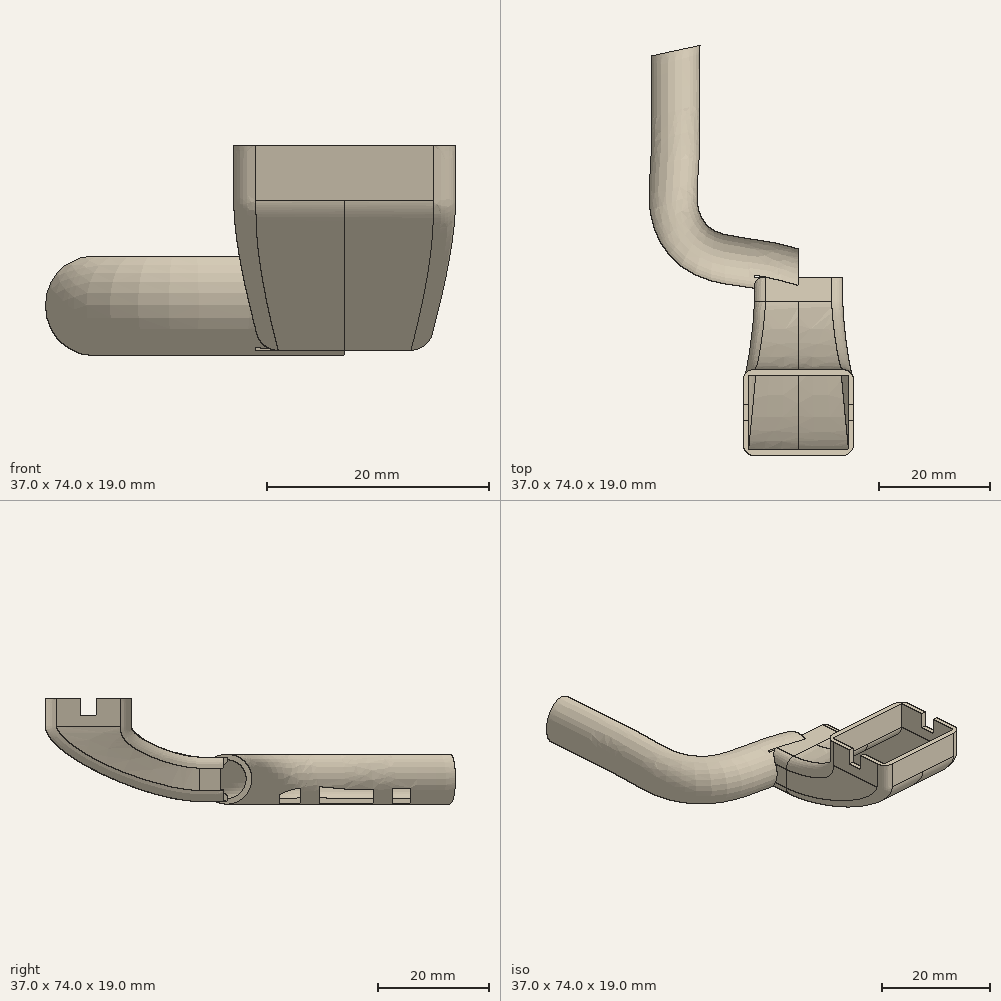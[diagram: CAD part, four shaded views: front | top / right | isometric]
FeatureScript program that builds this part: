
annotation { "Feature Type Name" : "Feature", "Feature Type Description" : "" }
export const myFeature = defineFeature(function(context is Context, id is Id, definition is map)
    precondition{}
    {
        {
            var Q0;
            Q0=qCreatedBy(makeId("Top.planeOp"),FACE);
            var sketch = newSketch(context, id + "F0", { "sketchPlane" : qUnion([Q0])});
            skLineSegment(sketch, "E0.bottom", {"start": v(-10, -17.25) * mm, "end": v(0, -17.25) * mm});
            skLineSegment(sketch, "E0.top", {"start": v(-10, -32.75) * mm, "end": v(0, -32.75) * mm});
            skLineSegment(sketch, "E0.left", {"start": v(-10, -17.25) * mm, "end": v(-10, -32.75) * mm});
            skLineSegment(sketch, "E0.right", {"start": v(0, -17.25) * mm, "end": v(0, -32.75) * mm});
            skPoint(sketch, "E0.middle", {"position": v(-5, -25) * mm});
            skSolve(sketch);
        }
        {
            var Q0;
            Q0=qCreatedBy(makeId("Front.planeOp"),FACE);
            var sketch = newSketch(context, id + "F1", { "sketchPlane" : qUnion([Q0])});
            skLineSegment(sketch, "E1", {"start": v(-4.94, -14.5) * mm, "end": v(6.87, -14.5) * mm, "construction": true});
            skLineSegment(sketch, "E2.bottom", {"start": v(-8, -10.5) * mm, "end": v(0, -10.5) * mm});
            skLineSegment(sketch, "E2.top", {"start": v(-8, -18.5) * mm, "end": v(0, -18.5) * mm});
            skLineSegment(sketch, "E2.left", {"start": v(-8, -10.5) * mm, "end": v(-8, -18.5) * mm});
            skPoint(sketch, "E2.middle", {"position": v(0, -14.5) * mm});
            skLineSegment(sketch, "E3", {"start": v(0, 0) * mm, "end": v(0, -51.5) * mm, "construction": true});
            skPoint(sketch, "E3.endSnap0", {"position": v(0, -18.5) * mm});
            skLineSegment(sketch, "E4", {"start": v(0, -51.5) * mm, "end": v(0, 0) * mm, "construction": true});
            skLineSegment(sketch, "E5", {"start": v(0, 46.65) * mm, "end": v(0, 0) * mm, "construction": true});
            skLineSegment(sketch, "E6", {"start": v(0, -10.5) * mm, "end": v(0, -18.5) * mm});
            skPoint(sketch, "E7.orphan", {"position": v(8, -10.5) * mm});
            skPoint(sketch, "E8.orphan", {"position": v(8, -18.5) * mm});
            skSolve(sketch);
        }
        {
            var Q0;
            Q0=qCreatedBy(makeId("Right.planeOp"),FACE);
            var sketch = newSketch(context, id + "F2", { "sketchPlane" : qUnion([Q0])});
            skCircle(sketch, "E9", {"center": v(0, -14.5) * mm, "radius": 4.5 * mm});
            skSolve(sketch);
        }
        {
            var Q0;
            Q0=sQuery(id+"F1.wireOp",EDGE,"E1");
            cPlane(context, id + "F3", {"entities" : qUnion([Q0]), "cplaneType" : CPlaneType.LINE_ANGLE, "offset" : 25 * mm, "angle" : 90 * degree, "width" : 150 * mm, "height" : 150 * mm});
        }
        {
            var Q0;
            Q0=qCreatedBy(id+"F3.planeOp",FACE);
            var sketch = newSketch(context, id + "F4", { "sketchPlane" : qUnion([Q0])});
            skFitSpline(sketch, "E10", {"points": [v(0, 0) * mm, v(-3.6, 0.99) * mm, v(-9.1, 2) * mm, v(-17.4, 4.14) * mm, v(-22.17, 10.6) * mm, v(-22.33, 20.29) * mm, v(-22.17, 29.36) * mm, v(-22.17, 36.59) * mm, v(-22.17, 40.28) * mm], "startDerivative": vector(-34.67, 9.15) * mm, "endDerivative": vector(2.11, 46.5) * mm});
            skLineSegment(sketch, "E11", {"start": v(0, 0) * mm, "end": v(0, 49.73) * mm, "construction": true});
            skSolve(sketch);
        }
        {
            var Q0;
            Q0=sQuery(id+"F4.wireOp",VERTEX,"E10.8.internal");
            var Q1;
            Q1=sQuery(id+"F4.wireOp",EDGE,"E11");
            cPlane(context, id + "F5", {"entities" : qUnion([Q0, Q1]), "cplaneType" : CPlaneType.LINE_POINT, "offset" : 25 * mm, "width" : 150 * mm, "height" : 150 * mm});
        }
        {
            var Q0;
            Q0=sQuery(id+"F1.wireOp",EDGE,"E2.bottom");
            cPlane(context, id + "F6", {"entities" : qUnion([Q0]), "cplaneType" : CPlaneType.LINE_ANGLE, "offset" : 25 * mm, "angle" : 27.84 * degree, "width" : 150 * mm, "height" : 150 * mm});
        }
        {
            var Q0;
            Q0 = qSketchRegion(id + "F0", true);
            extrude(context, id + "F7", {"entities" : qUnion([Q0]), "oppositeDirection" : true, "depth" : 5 * mm});
        }
        {
            var Q0;
            Q0=makeQuery(id+"F2.imprint","IMPRINT",FACE,{"disambiguationData":[TD([[makeQuery(id+"F2.imprint","IMPRINT",EDGE,{"derivedFrom":sQuery(id+"F2.wireOp",EDGE,"E9")}),1.0]])]});
            var Q1;
            Q1=sQuery(id+"F2.wireOp",EDGE,"E9");
            var Q2;
            Q2=sQuery(id+"F4.wireOp",EDGE,"E10");
            sweep(context, id + "F8", {"profiles" : qUnion([Q0]), "surfaceProfiles" : qUnion([Q1]), "path" : qUnion([Q2])});
        }
        {
            var Q0;
            Q0 = qSketchRegion(id + "F1", true);
            extrude(context, id + "F9", {"entities" : qUnion([Q0]), "depth" : 5 * mm});
        }
        {
            var Q0;
            Q0=makeQuery(id+"F9.opExtrude","SWEPT_FACE",FACE,{"disambiguationData":[OSD([sQuery(id+"F1.wireOp",EDGE,"E6")])]});
            var Q1;
            Q1=makeQuery(id+"F9.opExtrude","CAP_FACE",FACE,{"disambiguationData":[OSD([sQuery(id+"F1.wireOp",EDGE,"E2.bottom"),sQuery(id+"F1.wireOp",EDGE,"E2.top"),sQuery(id+"F1.wireOp",EDGE,"E2.left"),sQuery(id+"F1.wireOp",EDGE,"E6")])],"isStart":true});
            var Q2;
            Q2=makeQuery(id+"F9.opExtrude","SWEPT_BODY",BODY,{"disambiguationData":[OSD([sQuery(id+"F1.wireOp",EDGE,"E2.bottom"),sQuery(id+"F1.wireOp",EDGE,"E2.top"),sQuery(id+"F1.wireOp",EDGE,"E2.left"),sQuery(id+"F1.wireOp",EDGE,"E6")])]});
            shell(context, id + "F10", {"entities" : qUnion([Q0, Q1]), "parts" : qUnion([Q2]), "thickness" : 1 * mm});
        }
        {
            var Q0;
            Q0=makeQuery(id+"F7.opExtrude","CAP_FACE",FACE,{"disambiguationData":[OSD([sQuery(id+"F0.wireOp",EDGE,"E0.bottom"),sQuery(id+"F0.wireOp",EDGE,"E0.top"),sQuery(id+"F0.wireOp",EDGE,"E0.left"),sQuery(id+"F0.wireOp",EDGE,"E0.right")])],"isStart":false});
            var Q1;
            Q1=makeQuery(id+"F9.opExtrude","CAP_FACE",FACE,{"disambiguationData":[OSD([sQuery(id+"F1.wireOp",EDGE,"E2.bottom"),sQuery(id+"F1.wireOp",EDGE,"E2.top"),sQuery(id+"F1.wireOp",EDGE,"E2.left"),sQuery(id+"F1.wireOp",EDGE,"E6")])],"isStart":false});
            loft(context, id + "F11", {"startCondition" : LoftEndDerivativeType.NORMAL_TO_PROFILE, "startMagnitude" : 1, "endCondition" : LoftEndDerivativeType.NORMAL_TO_PROFILE, "endMagnitude" : 1, "sheetProfilesArray" : [{ "sheetProfileEntities" : qUnion([Q0]) }, { "sheetProfileEntities" : qUnion([Q1]) }]});
        }
        {
            var Q0;
            Q0=makeQuery(id+"F8.opSweep","CAP_FACE",FACE,{"disambiguationData":[OSD([sQuery(id+"F2.wireOp",EDGE,"E9"),sQuery(id+"F4.wireOp",VERTEX,"E10.start")])],"isStart":true});
            shell(context, id + "F12", {"entities" : qUnion([Q0]), "thickness" : 1 * mm});
        }
        {
            var Q0;
            Q0=makeQuery(id+"F1.imprint","IMPRINT",FACE,{"disambiguationData":[TD([[makeQuery(id+"F1.imprint","IMPRINT",EDGE,{"derivedFrom":sQuery(id+"F1.wireOp",EDGE,"E2.bottom")}),-1.0]])]});
            extrude(context, id + "F13", {"entities" : qUnion([Q0]), "operationType" : NewBodyOperationType.REMOVE, "depth" : 0.6 * mm});
        }
        {
            var Q0;
            Q0=makeQuery(id+"F7.opExtrude","SWEPT_BODY",BODY,{"disambiguationData":[OSD([sQuery(id+"F0.wireOp",EDGE,"E0.bottom"),sQuery(id+"F0.wireOp",EDGE,"E0.top"),sQuery(id+"F0.wireOp",EDGE,"E0.left"),sQuery(id+"F0.wireOp",EDGE,"E0.right")])]});
            var Q1;
            Q1=makeQuery(id+"F11.opLoft","SWEPT_BODY",BODY,{"disambiguationData":[OSD([sQuery(id+"F0.wireOp",EDGE,"E0.bottom"),sQuery(id+"F0.wireOp",EDGE,"E0.top"),sQuery(id+"F0.wireOp",EDGE,"E0.left"),sQuery(id+"F0.wireOp",EDGE,"E0.right"),sQuery(id+"F1.wireOp",EDGE,"E2.bottom"),sQuery(id+"F1.wireOp",EDGE,"E2.top"),sQuery(id+"F1.wireOp",EDGE,"E2.left"),sQuery(id+"F1.wireOp",EDGE,"E6")])]});
            var Q2;
            Q2=makeQuery(id+"F9.opExtrude","SWEPT_BODY",BODY,{"disambiguationData":[OSD([sQuery(id+"F1.wireOp",EDGE,"E2.bottom"),sQuery(id+"F1.wireOp",EDGE,"E2.top"),sQuery(id+"F1.wireOp",EDGE,"E2.left"),sQuery(id+"F1.wireOp",EDGE,"E6")])]});
            booleanBodies(context, id + "F14", {"operationType" : BooleanOperationType.UNION, "tools" : qUnion([Q0, Q1, Q2])});
        }
        {
            var Q0;
            {var subQ0=sQuery(id+"F1.wireOp",EDGE,"E6");var subQ1=sQuery(id+"F0.wireOp",EDGE,"E0.right");Q0=makeQuery(id+"F14.opBoolean","MERGE",FACE,{"derivedFrom":[makeQuery(id+"F7.opExtrude","SWEPT_FACE",FACE,{"disambiguationData":[OSD([subQ1])]}),makeQuery(id+"F11.opLoft","SWEPT_FACE",FACE,{"disambiguationData":[OSD([sQuery(id+"F0.wireOp",EDGE,"E0.bottom"),sQuery(id+"F0.wireOp",EDGE,"E0.top"),subQ1,sQuery(id+"F1.wireOp",EDGE,"E2.bottom"),sQuery(id+"F1.wireOp",EDGE,"E2.top"),subQ0])]}),makeQuery(id+"F9.opExtrude","SWEPT_FACE",FACE,{"disambiguationData":[OSD([subQ0])]})]});}
            var Q1;
            Q1=makeQuery(id+"F10.opShell","OFFSET_FACE",FACE,{"disambiguationData":[OSD([sQuery(id+"F1.wireOp",EDGE,"E2.bottom"),sQuery(id+"F1.wireOp",EDGE,"E2.top"),sQuery(id+"F1.wireOp",EDGE,"E2.left"),sQuery(id+"F1.wireOp",EDGE,"E6")])]});
            var Q2;
            Q2=makeQuery(id+"F7.opExtrude","CAP_FACE",FACE,{"disambiguationData":[OSD([sQuery(id+"F0.wireOp",EDGE,"E0.bottom"),sQuery(id+"F0.wireOp",EDGE,"E0.top"),sQuery(id+"F0.wireOp",EDGE,"E0.left"),sQuery(id+"F0.wireOp",EDGE,"E0.right")])],"isStart":true});
            shell(context, id + "F15", {"entities" : qUnion([Q0, Q1, Q2]), "thickness" : 1 * mm});
        }
        {
            var Q0;
            Q0=makeQuery(id+"F13.boolean.opBoolean","COPY",FACE,{"derivedFrom":makeQuery(id+"F13.opExtrude","CAP_FACE",FACE,{"disambiguationData":[OSD([sQuery(id+"F1.wireOp",EDGE,"E2.bottom"),sQuery(id+"F1.wireOp",EDGE,"E2.top"),sQuery(id+"F1.wireOp",EDGE,"E2.left"),sQuery(id+"F1.wireOp",EDGE,"E6")])],"isStart":false})});
            var sketch = newSketch(context, id + "F16", { "sketchPlane" : qUnion([Q0])});
            skLineSegment(sketch, "E12.bottom", {"start": v(7, -12.6) * mm, "end": v(8, -12.6) * mm});
            skLineSegment(sketch, "E12.top", {"start": v(7, -12.68) * mm, "end": v(8, -12.68) * mm});
            skLineSegment(sketch, "E12.left", {"start": v(7, -12.6) * mm, "end": v(7, -12.68) * mm});
            skLineSegment(sketch, "E12.right", {"start": v(8, -12.6) * mm, "end": v(8, -12.68) * mm});
            skLineSegment(sketch, "E13.bottom", {"start": v(8, -16.37) * mm, "end": v(7, -16.37) * mm});
            skLineSegment(sketch, "E13.top", {"start": v(8, -16.28) * mm, "end": v(7, -16.28) * mm});
            skLineSegment(sketch, "E13.left", {"start": v(8, -16.37) * mm, "end": v(8, -16.28) * mm});
            skLineSegment(sketch, "E13.right", {"start": v(7, -16.37) * mm, "end": v(7, -16.28) * mm});
            skLineSegment(sketch, "E14", {"start": v(7, -16.28) * mm, "end": v(7, -12.68) * mm});
            skLineSegment(sketch, "E15", {"start": v(8, -12.6) * mm, "end": v(8, -16.28) * mm});
            skSolve(sketch);
        }
        {
            var Q0;
            Q0 = qSketchRegion(id + "F16", true);
            extrude(context, id + "F17", {"entities" : qUnion([Q0]), "operationType" : NewBodyOperationType.REMOVE, "oppositeDirection" : true, "depth" : 0.5 * mm});
        }
        {
            var Q0;
            Q0=makeQuery(id+"F2.imprint","IMPRINT",FACE,{"disambiguationData":[TD([[makeQuery(id+"F2.imprint","IMPRINT",EDGE,{"derivedFrom":sQuery(id+"F2.wireOp",EDGE,"E9")}),1.0]])]});
            var sketch = newSketch(context, id + "F18", { "sketchPlane" : qUnion([Q0])});
            skLineSegment(sketch, "E16", {"start": v(-4.73, -11.46) * mm, "end": v(-0.8, -11.46) * mm});
            skLineSegment(sketch, "E17", {"start": v(-0.8, -11.46) * mm, "end": v(-0.8, -17.5) * mm});
            skLineSegment(sketch, "E18", {"start": v(-0.8, -17.5) * mm, "end": v(-4.72, -17.5) * mm});
            skLineSegment(sketch, "E19", {"start": v(-4.72, -17.5) * mm, "end": v(-4.72, -11.46) * mm});
            skSolve(sketch);
        }
        {
            var Q0;
            Q0 = qSketchRegion(id + "F18", true);
            extrude(context, id + "F19", {"entities" : qUnion([Q0]), "operationType" : NewBodyOperationType.REMOVE, "oppositeDirection" : true, "depth" : 7 * mm});
        }
        {
            var Q0;
            Q0=sQuery(id+"F1.wireOp",VERTEX,"E2.middle");
            var Q1;
            Q1=sQuery(id+"F4.wireOp",VERTEX,"E10.8.internal");
            var Q2;
            Q2=sQuery(id+"F4.wireOp",VERTEX,"E11.end");
            cPlane(context, id + "F20", {"entities" : qUnion([Q0, Q1, Q2]), "cplaneType" : CPlaneType.THREE_POINT, "offset" : 25 * mm, "oppositeDirection" : true, "width" : 150 * mm, "height" : 150 * mm});
        }
        {
            var Q0;
            Q0=qCreatedBy(id+"F20.planeOp",FACE);
            var sketch = newSketch(context, id + "F21", { "sketchPlane" : qUnion([Q0])});
            skLineSegment(sketch, "E20.bottom", {"start": v(-24.12, 33.19) * mm, "end": v(-20.15, 33.19) * mm});
            skLineSegment(sketch, "E20.top", {"start": v(-24.12, 29.87) * mm, "end": v(-20.15, 29.87) * mm});
            skLineSegment(sketch, "E20.left", {"start": v(-24.12, 33.19) * mm, "end": v(-24.12, 29.87) * mm});
            skLineSegment(sketch, "E20.right", {"start": v(-20.15, 33.19) * mm, "end": v(-20.15, 29.87) * mm});
            skPoint(sketch, "E20.middle", {"position": v(-22.13, 31.53) * mm});
            skLineSegment(sketch, "E21.bottom", {"start": v(-24.12, 26.45) * mm, "end": v(-20.37, 26.45) * mm});
            skLineSegment(sketch, "E21.top", {"start": v(-24.12, 16.73) * mm, "end": v(-20.37, 16.73) * mm});
            skLineSegment(sketch, "E21.left", {"start": v(-24.12, 26.45) * mm, "end": v(-24.12, 16.73) * mm});
            skLineSegment(sketch, "E21.right", {"start": v(-20.37, 26.45) * mm, "end": v(-20.37, 16.73) * mm});
            skPoint(sketch, "E21.middle", {"position": v(-22.25, 21.59) * mm});
            skLineSegment(sketch, "E22.bottom", {"start": v(-24.12, 13.3) * mm, "end": v(-20.59, 13.3) * mm});
            skLineSegment(sketch, "E22.top", {"start": v(-24.12, 9.55) * mm, "end": v(-20.59, 9.55) * mm});
            skLineSegment(sketch, "E22.left", {"start": v(-24.12, 13.3) * mm, "end": v(-24.12, 9.55) * mm});
            skLineSegment(sketch, "E22.right", {"start": v(-20.59, 13.3) * mm, "end": v(-20.59, 9.55) * mm});
            skPoint(sketch, "E22.middle", {"position": v(-22.36, 11.43) * mm});
            skSolve(sketch);
        }
        {
            var Q0;
            Q0 = qSketchRegion(id + "F21", true);
            extrude(context, id + "F22", {"entities" : qUnion([Q0]), "oppositeDirection" : true, "depth" : 7 * mm});
        }
        {
            var Q0;
            Q0=makeQuery(id+"F22.opExtrude","SWEPT_BODY",BODY,{"disambiguationData":[OSD([sQuery(id+"F21.wireOp",EDGE,"E22.bottom"),sQuery(id+"F21.wireOp",EDGE,"E22.top"),sQuery(id+"F21.wireOp",EDGE,"E22.left"),sQuery(id+"F21.wireOp",EDGE,"E22.right")])]});
            var Q1;
            Q1=makeQuery(id+"F22.opExtrude","SWEPT_BODY",BODY,{"disambiguationData":[OSD([sQuery(id+"F21.wireOp",EDGE,"E20.bottom"),sQuery(id+"F21.wireOp",EDGE,"E20.top"),sQuery(id+"F21.wireOp",EDGE,"E20.left"),sQuery(id+"F21.wireOp",EDGE,"E20.right")])]});
            var Q2;
            Q2=makeQuery(id+"F22.opExtrude","SWEPT_BODY",BODY,{"disambiguationData":[OSD([sQuery(id+"F21.wireOp",EDGE,"E21.bottom"),sQuery(id+"F21.wireOp",EDGE,"E21.top"),sQuery(id+"F21.wireOp",EDGE,"E21.left"),sQuery(id+"F21.wireOp",EDGE,"E21.right")])]});
            var Q3;
            Q3=makeQuery(id+"F22.opExtrude","CAP_EDGE",EDGE,{"disambiguationData":[OSD([sQuery(id+"F21.wireOp",EDGE,"E21.right")])],"isStart":false});
            transform(context, id + "F23", {"entities" : qUnion([Q0, Q1, Q2]), "transformType" : TransformType.ROTATION, "transformAxis" : qUnion([Q3]), "angle" : 20 * degree, "makeCopy" : false});
        }
        {
            var Q0;
            Q0=makeQuery(id+"F22.opExtrude","SWEPT_BODY",BODY,{"disambiguationData":[OSD([sQuery(id+"F21.wireOp",EDGE,"E22.bottom"),sQuery(id+"F21.wireOp",EDGE,"E22.top"),sQuery(id+"F21.wireOp",EDGE,"E22.left"),sQuery(id+"F21.wireOp",EDGE,"E22.right")])]});
            var Q1;
            Q1=makeQuery(id+"F22.opExtrude","SWEPT_BODY",BODY,{"disambiguationData":[OSD([sQuery(id+"F21.wireOp",EDGE,"E21.bottom"),sQuery(id+"F21.wireOp",EDGE,"E21.top"),sQuery(id+"F21.wireOp",EDGE,"E21.left"),sQuery(id+"F21.wireOp",EDGE,"E21.right")])]});
            var Q2;
            Q2=makeQuery(id+"F22.opExtrude","SWEPT_BODY",BODY,{"disambiguationData":[OSD([sQuery(id+"F21.wireOp",EDGE,"E20.bottom"),sQuery(id+"F21.wireOp",EDGE,"E20.top"),sQuery(id+"F21.wireOp",EDGE,"E20.left"),sQuery(id+"F21.wireOp",EDGE,"E20.right")])]});
            transform(context, id + "F24", {"entities" : qUnion([Q0, Q1, Q2]), "transformType" : TransformType.TRANSLATION_3D, "dx" : 4 * mm, "dy" : 0 * mm, "dz" : 0 * mm, "makeCopy" : false});
        }
        {
            var Q0;
            Q0=makeQuery(id+"F22.opExtrude","SWEPT_BODY",BODY,{"disambiguationData":[OSD([sQuery(id+"F21.wireOp",EDGE,"E20.bottom"),sQuery(id+"F21.wireOp",EDGE,"E20.top"),sQuery(id+"F21.wireOp",EDGE,"E20.left"),sQuery(id+"F21.wireOp",EDGE,"E20.right")])]});
            var Q1;
            Q1=makeQuery(id+"F22.opExtrude","SWEPT_BODY",BODY,{"disambiguationData":[OSD([sQuery(id+"F21.wireOp",EDGE,"E21.bottom"),sQuery(id+"F21.wireOp",EDGE,"E21.top"),sQuery(id+"F21.wireOp",EDGE,"E21.left"),sQuery(id+"F21.wireOp",EDGE,"E21.right")])]});
            var Q2;
            Q2=makeQuery(id+"F22.opExtrude","SWEPT_BODY",BODY,{"disambiguationData":[OSD([sQuery(id+"F21.wireOp",EDGE,"E22.bottom"),sQuery(id+"F21.wireOp",EDGE,"E22.top"),sQuery(id+"F21.wireOp",EDGE,"E22.left"),sQuery(id+"F21.wireOp",EDGE,"E22.right")])]});
            var Q3;
            Q3=makeQuery(id+"F8.opSweep","SWEPT_BODY",BODY,{"disambiguationData":[OSD([sQuery(id+"F2.wireOp",EDGE,"E9"),sQuery(id+"F4.wireOp",EDGE,"E10")])]});
            booleanBodies(context, id + "F25", {"operationType" : BooleanOperationType.SUBTRACTION, "tools" : qUnion([Q0, Q1, Q2]), "targets" : qUnion([Q3])});
        }
        {
            var Q0;
            Q0=makeQuery(id+"F7.opExtrude","SWEPT_BODY",BODY,{"disambiguationData":[OSD([sQuery(id+"F0.wireOp",EDGE,"E0.bottom"),sQuery(id+"F0.wireOp",EDGE,"E0.top"),sQuery(id+"F0.wireOp",EDGE,"E0.left"),sQuery(id+"F0.wireOp",EDGE,"E0.right")])]});
            var Q1;
            Q1=qCreatedBy(makeId("Right.planeOp"),FACE);
            mirror(context, id + "F26", {"operationType" : NewBodyOperationType.ADD, "entities" : qUnion([Q0]), "mirrorPlane" : qUnion([Q1])});
        }
        {
            var Q0;
            Q0=makeQuery(id+"F0.imprint","IMPRINT",FACE,{"disambiguationData":[TD([[makeQuery(id+"F0.imprint","IMPRINT",EDGE,{"derivedFrom":sQuery(id+"F0.wireOp",EDGE,"E0.bottom")}),-1.0]])]});
            var sketch = newSketch(context, id + "F27", { "sketchPlane" : qUnion([Q0])});
            skLineSegment(sketch, "E23.bottom", {"start": v(-12.05, -23.5) * mm, "end": v(12.05, -23.5) * mm});
            skLineSegment(sketch, "E23.top", {"start": v(-12.05, -26.5) * mm, "end": v(12.05, -26.5) * mm});
            skLineSegment(sketch, "E23.left", {"start": v(-12.05, -23.5) * mm, "end": v(-12.05, -26.5) * mm});
            skLineSegment(sketch, "E23.right", {"start": v(12.05, -23.5) * mm, "end": v(12.05, -26.5) * mm});
            skPoint(sketch, "E23.middle", {"position": v(0, -25) * mm});
            skSolve(sketch);
        }
        {
            var Q0;
            Q0 = qSketchRegion(id + "F27", true);
            extrude(context, id + "F28", {"entities" : qUnion([Q0]), "operationType" : NewBodyOperationType.REMOVE, "oppositeDirection" : true, "depth" : 3 * mm});
        }
        {
            var Q0;
            Q0=makeQuery(id+"F11.opLoft","SWEPT_EDGE",EDGE,{"disambiguationData":[OSD([sQuery(id+"F0.wireOp",EDGE,"E0.top"),sQuery(id+"F0.wireOp",EDGE,"E0.left"),sQuery(id+"F1.wireOp",EDGE,"E2.top"),sQuery(id+"F1.wireOp",EDGE,"E2.left")])]});
            var Q1;
            Q1=makeQuery(id+"F26.opPattern","COPY",EDGE,{"derivedFrom":makeQuery(id+"F11.opLoft","SWEPT_EDGE",EDGE,{"disambiguationData":[OSD([sQuery(id+"F0.wireOp",EDGE,"E0.top"),sQuery(id+"F0.wireOp",EDGE,"E0.left"),sQuery(id+"F1.wireOp",EDGE,"E2.top"),sQuery(id+"F1.wireOp",EDGE,"E2.left")])]}),"instanceName":"1"});
            var Q2;
            Q2=makeQuery(id+"F26.opPattern","COPY",EDGE,{"derivedFrom":makeQuery(id+"F11.opLoft","SWEPT_EDGE",EDGE,{"disambiguationData":[OSD([sQuery(id+"F0.wireOp",EDGE,"E0.bottom"),sQuery(id+"F0.wireOp",EDGE,"E0.left"),sQuery(id+"F1.wireOp",EDGE,"E2.bottom"),sQuery(id+"F1.wireOp",EDGE,"E2.left")])]}),"instanceName":"1"});
            var Q3;
            Q3=makeQuery(id+"F11.opLoft","SWEPT_EDGE",EDGE,{"disambiguationData":[OSD([sQuery(id+"F0.wireOp",EDGE,"E0.bottom"),sQuery(id+"F0.wireOp",EDGE,"E0.left"),sQuery(id+"F1.wireOp",EDGE,"E2.bottom"),sQuery(id+"F1.wireOp",EDGE,"E2.left")])]});
            var Q4;
            {var subQ0=sQuery(id+"F0.wireOp",EDGE,"E0.bottom");Q4=makeQuery(id+"F14.opBoolean","MERGE",EDGE,{"derivedFrom":[makeQuery(id+"F7.opExtrude","CAP_EDGE",EDGE,{"disambiguationData":[OSD([subQ0])],"isStart":false}),makeQuery(id+"F11.opLoft","MID_CAP_EDGE",EDGE,{"disambiguationData":[OSD([subQ0,sQuery(id+"F0.wireOp",EDGE,"E0.left"),sQuery(id+"F0.wireOp",EDGE,"E0.right")])],"capPos":0.0})]});}
            fillet(context, id + "F29", {"entities" : qUnion([Q0, Q1, Q2, Q3, Q4]), "radius" : 2 * mm, "allowEdgeOverflow" : false});
        }
    });
